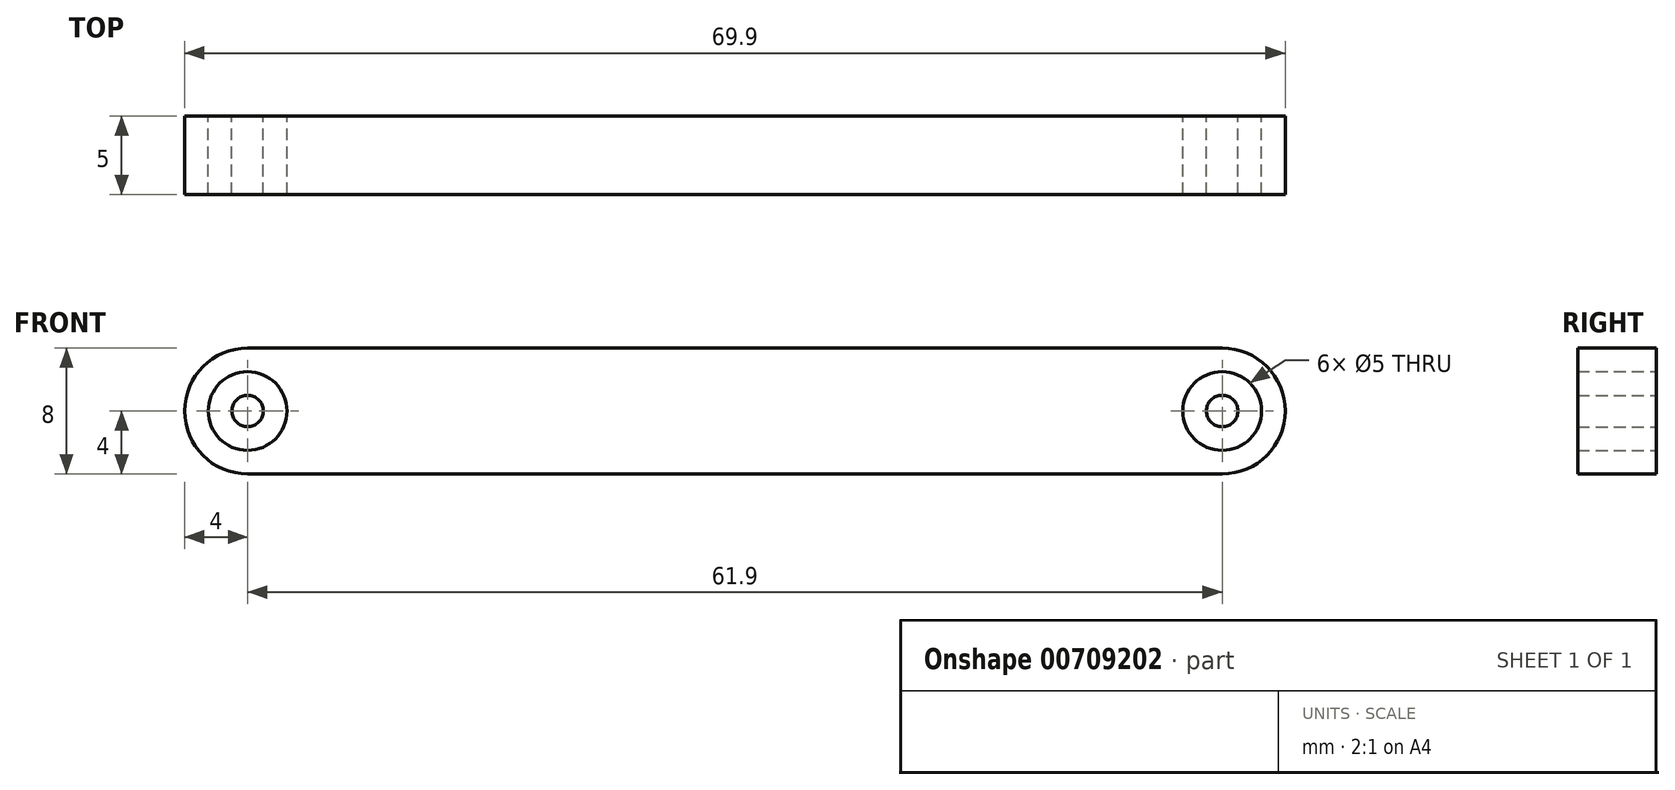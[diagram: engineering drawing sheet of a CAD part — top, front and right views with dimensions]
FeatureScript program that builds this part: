
annotation { "Feature Type Name" : "Feature", "Feature Type Description" : "" }
export const myFeature = defineFeature(function(context is Context, id is Id, definition is map)
    precondition{}
    {
        {
            var Q0;
            Q0=qCreatedBy(makeId("Front.planeOp"),FACE);
            var sketch = newSketch(context, id + "F0", { "sketchPlane" : qUnion([Q0])});
            skArc(sketch, "E0", {"start": v(0, 4) * mm, "mid": v(-4, 0) * mm, "end": v(0, -4) * mm});
            skArc(sketch, "E1", {"start": v(61.9, -4) * mm, "mid": v(65.9, 0) * mm, "end": v(61.9, 4) * mm});
            skLineSegment(sketch, "E2", {"start": v(0, 4) * mm, "end": v(61.9, 4) * mm});
            skLineSegment(sketch, "E3", {"start": v(0, -4) * mm, "end": v(61.9, -4) * mm});
            skCircle(sketch, "E4", {"center": v(0, 0) * mm, "radius": 2.5 * mm});
            skCircle(sketch, "E5", {"center": v(0, 0) * mm, "radius": 1 * mm});
            skCircle(sketch, "E6", {"center": v(61.9, 0) * mm, "radius": 2.5 * mm});
            skCircle(sketch, "E7", {"center": v(61.9, 0) * mm, "radius": 1 * mm});
            skSolve(sketch);
        }
        {
            var Q0;
            Q0=makeQuery(id+"F0.imprint","IMPRINT",FACE,{"disambiguationData":[TD([[makeQuery(id+"F0.imprint","IMPRINT",EDGE,{"derivedFrom":sQuery(id+"F0.wireOp",EDGE,"E0")}),1.0]])]});
            var Q1;
            Q1=makeQuery(id+"F0.imprint","IMPRINT",FACE,{"disambiguationData":[TD([[makeQuery(id+"F0.imprint","IMPRINT",EDGE,{"derivedFrom":sQuery(id+"F0.wireOp",EDGE,"E5")}),1.0]])]});
            var Q2;
            Q2=makeQuery(id+"F0.imprint","IMPRINT",FACE,{"disambiguationData":[TD([[makeQuery(id+"F0.imprint","IMPRINT",EDGE,{"derivedFrom":sQuery(id+"F0.wireOp",EDGE,"E7")}),1.0]])]});
            extrude(context, id + "F1", {"entities" : qUnion([Q0, Q1, Q2]), "depth" : 5 * mm, "offsetDistance" : 25 * mm});
        }
    });
